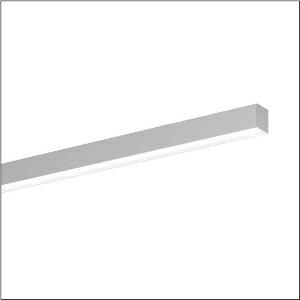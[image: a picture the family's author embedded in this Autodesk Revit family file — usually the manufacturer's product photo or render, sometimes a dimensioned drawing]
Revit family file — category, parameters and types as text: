
# Revit family: silica_r__21_51mx23tbt5s_3fb0
name_source: partatom
category: Lighting Fixtures
units: mm (PartAtom-declared; Revit-internal decimal feet)

## family parameters
Cut with Voids When Loaded = No
Host = Face
Light Source = No
Part Type = Normal
Room Calculation Point = No
Round Connector Dimension = Use Diameter
Shared = No

## types (1)
- --- (1 x LED, 4030 lm, 40.5 W, 6500K)
    Apparent Load = 41 VA
    CIE Flux Codes = 78 96 99 100 100
    Color Rendering = 80
    Color Temperature = 6500K
    Default Elevation = 1800 mm
    Description = Silica® 21, office luminaire, primary optical cover: prismatic diffuser, of PMMA, CAT 2 (L<= 3000cd/m²), light emission: direct distribution, primary light characteristic: symmetric, installation type: surface-mounted, LED, rated luminous flux: 4.030lm, luminous efficacy: 95lm/W, light colour: 8tw, colour temperature: 2700..6500K, control gear: ECG DALI, with terminal, 3+2-pole, max. 2.5mm², mains connection: 220..240V, AC, 50/60Hz, rated input power: 42.6W, luminaire housing, of aluminium, metallic grey (RAL 9006), length: 1.504mm, width: 53mm, height: 53mm, protection rating (complete): IP20, insulation class (complete): insulation class I (protective earthing), certification: CE, permissible operating ambient temperature: 0..+35°C, standard: EN 50419, packaging unit: 1 piece
    Height = 0 mm  [stored 0 ft]
    Lamp = 1 x LED
    Lamp Light Flux = 4030 lm
    Lamp Power = 40.5 W
    Lamp count = 1
    Length = 1504 mm
    Luminous efficacy = 100 lm/W
    Manufacturer = Siteco
    ModVariant = No
    Model = 51MX23TBT5S
    Mounting Place = Ceiling
    Mounting Type = Recessed
    Number of Poles = 1
    OnlyDefault = Yes
    Power Factor = 1
    Product Name = Silica® 21
    Product group = office luminaire | ceiling recessed
    ProductGroupID = 401
    Protection Class = Protection class I
    Protection Degree = IP 20
    RLX_Detail_Level = 1
    RLX_Emergency_Light_Flux = 0 lm
    RLX_Emergency_Type = 0
    RLX_Emergency_Type_DB = No
    RlxData = <blob elided: 17997 chars, md5=d0b8ef92>
    Socket = socket
    Standby Power = 0 W
    System Light Flux = 4030 lm
    System Power = 41 W
    Type Comments = individual setting
    Type Image = l_1297768.jpg
    URL = http://relux.com
    VarID = @adj_071119
    Voltage = 0 V
    Weight = 0.00 kg
    Width = 53 mm

note: [stored X ft] marks values corroborated as IEEE doubles in the binary element streams (Revit-internal decimal feet)

## geometry (parser evidence)
native form markers: Blend x4, Sweep x10
no freeform markers — native parametric forms only
